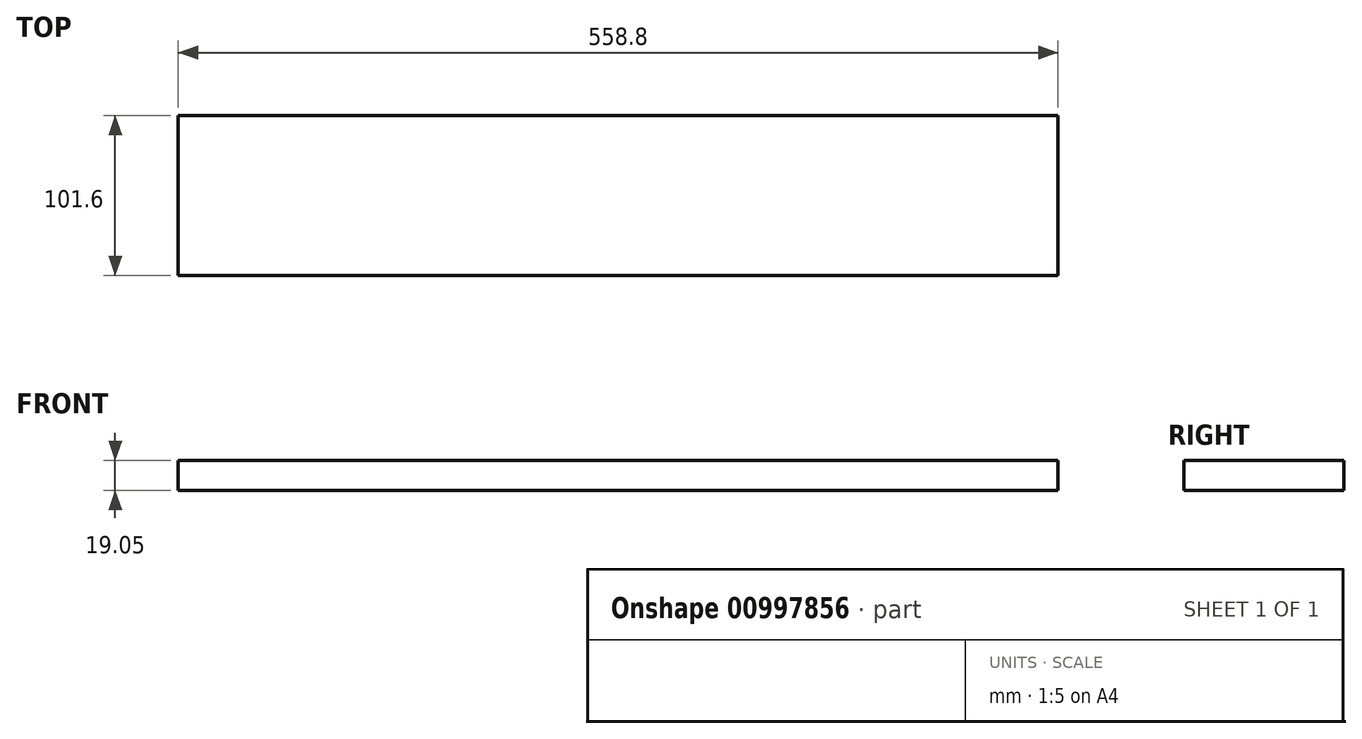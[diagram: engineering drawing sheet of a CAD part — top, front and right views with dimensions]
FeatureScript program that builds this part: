
annotation { "Feature Type Name" : "Feature", "Feature Type Description" : "" }
export const myFeature = defineFeature(function(context is Context, id is Id, definition is map)
    precondition{}
    {
        {
            var Q0;
            Q0=qCreatedBy(makeId("Top.planeOp"),FACE);
            var sketch = newSketch(context, id + "F0", { "sketchPlane" : qUnion([Q0])});
            skLineSegment(sketch, "E0.bottom", {"start": v(279.4, -50.8) * mm, "end": v(-279.4, -50.8) * mm});
            skLineSegment(sketch, "E0.top", {"start": v(279.4, 50.8) * mm, "end": v(-279.4, 50.8) * mm});
            skLineSegment(sketch, "E0.left", {"start": v(279.4, -50.8) * mm, "end": v(279.4, 50.8) * mm});
            skLineSegment(sketch, "E0.right", {"start": v(-279.4, -50.8) * mm, "end": v(-279.4, 50.8) * mm});
            skPoint(sketch, "E0.middle", {"position": v(0, 0) * mm});
            skSolve(sketch);
        }
        {
            var Q0;
            Q0=makeQuery(id+"F0.imprint","IMPRINT",FACE,{"disambiguationData":[TD([[makeQuery(id+"F0.imprint","IMPRINT",EDGE,{"derivedFrom":sQuery(id+"F0.wireOp",EDGE,"E0.bottom")}),-1.0]])]});
            extrude(context, id + "F1", {"entities" : qUnion([Q0]), "depth" : 19.05 * mm, "offsetDistance" : 25.4 * mm});
        }
    });
